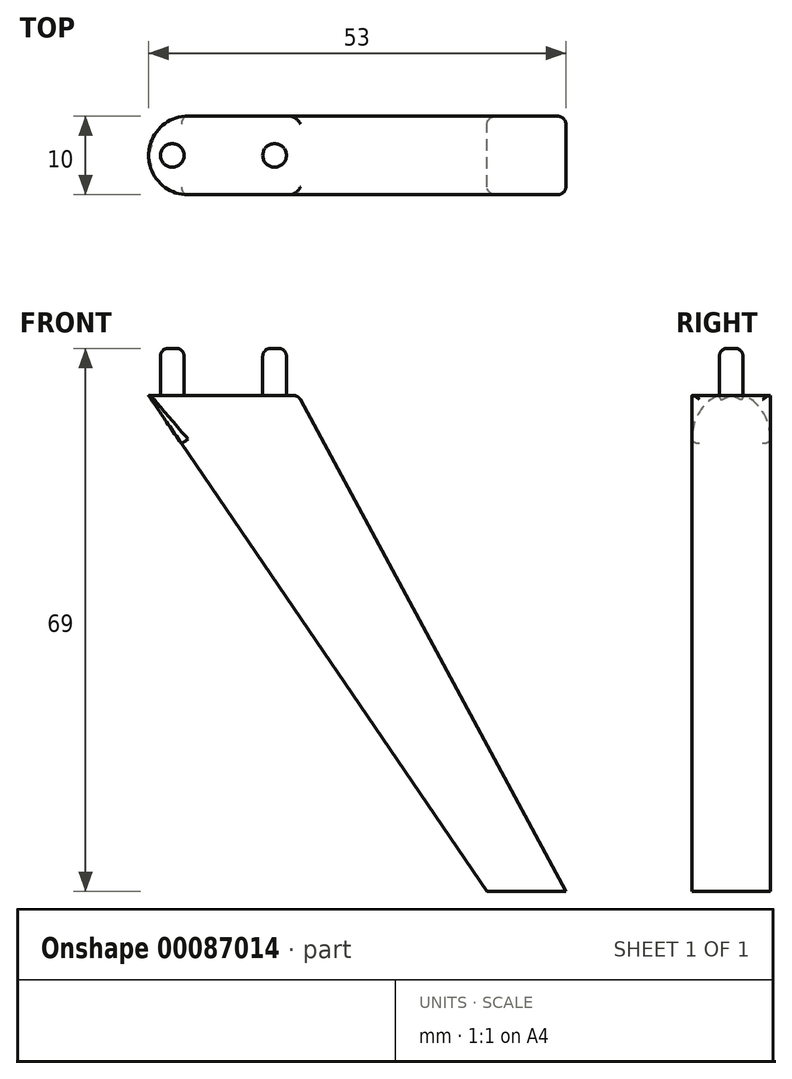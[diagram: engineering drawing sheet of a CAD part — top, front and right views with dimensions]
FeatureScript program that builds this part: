
annotation { "Feature Type Name" : "Feature", "Feature Type Description" : "" }
export const myFeature = defineFeature(function(context is Context, id is Id, definition is map)
    precondition{}
    {
        {
            var Q0;
            Q0=qCreatedBy(makeId("Front.planeOp"),FACE);
            var sketch = newSketch(context, id + "F0", { "sketchPlane" : qUnion([Q0])});
            skLineSegment(sketch, "E0.bottom", {"start": v(0, 0) * mm, "end": v(-53, 0) * mm, "construction": true});
            skLineSegment(sketch, "E0.top", {"start": v(0, 63) * mm, "end": v(-53, 63) * mm, "construction": true});
            skLineSegment(sketch, "E0.left", {"start": v(0, 0) * mm, "end": v(0, 63) * mm, "construction": true});
            skLineSegment(sketch, "E0.right", {"start": v(-53, 0) * mm, "end": v(-53, 63) * mm, "construction": true});
            skLineSegment(sketch, "E1", {"start": v(-53, 63) * mm, "end": v(-34, 63) * mm});
            skLineSegment(sketch, "E2", {"start": v(0, 0) * mm, "end": v(-10, 0) * mm});
            skLineSegment(sketch, "E3", {"start": v(-10, 0) * mm, "end": v(-53, 63) * mm});
            skLineSegment(sketch, "E4", {"start": v(0, 0) * mm, "end": v(-34, 63) * mm});
            skSolve(sketch);
        }
        {
            var Q0;
            Q0=makeQuery(id+"F0.imprint","IMPRINT",FACE,{"disambiguationData":[TD([[makeQuery(id+"F0.imprint","IMPRINT",EDGE,{"derivedFrom":sQuery(id+"F0.wireOp",EDGE,"E1")}),-1.0]])]});
            extrude(context, id + "F1", {"entities" : qUnion([Q0]), "depth" : 10 * mm});
        }
        {
            var Q0;
            Q0=makeQuery(id+"F1.opExtrude","SWEPT_FACE",FACE,{"disambiguationData":[OSD([sQuery(id+"F0.wireOp",EDGE,"E1")])]});
            var sketch = newSketch(context, id + "F2", { "sketchPlane" : qUnion([Q0])});
            skLineSegment(sketch, "E5", {"start": v(-53, -5) * mm, "end": v(-34, -5) * mm, "construction": true});
            skPoint(sketch, "E6", {"position": v(-50, -5) * mm});
            skPoint(sketch, "E7", {"position": v(-37, -5) * mm});
            skCircle(sketch, "E8", {"center": v(-50, -5) * mm, "radius": 1.5 * mm});
            skCircle(sketch, "E9", {"center": v(-37, -5) * mm, "radius": 1.5 * mm});
            skSolve(sketch);
        }
        {
            var Q0;
            Q0=makeQuery(id+"F2.imprint","IMPRINT",FACE,{"disambiguationData":[TD([[makeQuery(id+"F2.imprint","IMPRINT",EDGE,{"derivedFrom":sQuery(id+"F2.wireOp",EDGE,"E8")}),1.0]])]});
            var Q1;
            Q1=makeQuery(id+"F2.imprint","IMPRINT",FACE,{"disambiguationData":[TD([[makeQuery(id+"F2.imprint","IMPRINT",EDGE,{"derivedFrom":sQuery(id+"F2.wireOp",EDGE,"E9")}),1.0]])]});
            extrude(context, id + "F3", {"entities" : qUnion([Q0, Q1]), "operationType" : NewBodyOperationType.ADD, "depth" : 6 * mm});
        }
        {
            var Q0;
            Q0=makeQuery(id+"F3.opExtrude","CAP_EDGE",EDGE,{"disambiguationData":[OSD([sQuery(id+"F2.wireOp",EDGE,"E8")])],"isStart":false});
            var Q1;
            Q1=makeQuery(id+"F3.opExtrude","CAP_EDGE",EDGE,{"disambiguationData":[OSD([sQuery(id+"F2.wireOp",EDGE,"E9")])],"isStart":false});
            fillet(context, id + "F4", {"entities" : qUnion([Q0, Q1]), "radius" : 1 * mm, "tangentPropagation" : true, "allowEdgeOverflow" : false});
        }
        {
            var Q0;
            Q0=makeQuery(id+"F1.opExtrude","SWEPT_FACE",FACE,{"disambiguationData":[OSD([sQuery(id+"F0.wireOp",EDGE,"E1")])]});
            var sketch = newSketch(context, id + "F5", { "sketchPlane" : qUnion([Q0])});
            skLineSegment(sketch, "E10", {"start": v(-50, -5) * mm, "end": v(-37, -5) * mm});
            skPoint(sketch, "E11", {"position": v(-48, -5) * mm});
            skArc(sketch, "E12", {"start": v(-48, 0) * mm, "mid": v(-53, -5) * mm, "end": v(-48, -10) * mm});
            skLineSegment(sketch, "E13", {"start": v(-48, 0) * mm, "end": v(-56.06, 0) * mm});
            skLineSegment(sketch, "E14", {"start": v(-56.06, 0) * mm, "end": v(-56.06, -10) * mm});
            skLineSegment(sketch, "E15", {"start": v(-56.06, -10) * mm, "end": v(-48, -10) * mm});
            skSolve(sketch);
        }
        {
            var Q0;
            Q0 = qSketchRegion(id + "F5", true);
            extrude(context, id + "F6", {"entities" : qUnion([Q0]), "operationType" : NewBodyOperationType.REMOVE, "oppositeDirection" : true, "depth" : 21.71 * mm});
        }
        {
            var Q0;
            Q0=makeQuery(id+"F1.opExtrude","CAP_EDGE",EDGE,{"disambiguationData":[OSD([sQuery(id+"F0.wireOp",EDGE,"E3")])],"isStart":false});
            var Q1;
            Q1=makeQuery(id+"F1.opExtrude","CAP_EDGE",EDGE,{"disambiguationData":[OSD([sQuery(id+"F0.wireOp",EDGE,"E3")])],"isStart":true});
            var Q2;
            Q2=makeQuery(id+"F1.opExtrude","CAP_EDGE",EDGE,{"disambiguationData":[OSD([sQuery(id+"F0.wireOp",EDGE,"E4")])],"isStart":false});
            var Q3;
            Q3=makeQuery(id+"F1.opExtrude","CAP_EDGE",EDGE,{"disambiguationData":[OSD([sQuery(id+"F0.wireOp",EDGE,"E4")])],"isStart":true});
            var Q4;
            Q4=makeQuery(id+"F1.opExtrude","SWEPT_EDGE",EDGE,{"disambiguationData":[OSD([sQuery(id+"F0.wireOp",EDGE,"E1"),sQuery(id+"F0.wireOp",EDGE,"E4")])]});
            fillet(context, id + "F7", {"entities" : qUnion([Q0, Q1, Q2, Q3, Q4]), "radius" : 1 * mm, "tangentPropagation" : true, "allowEdgeOverflow" : false});
        }
    });
